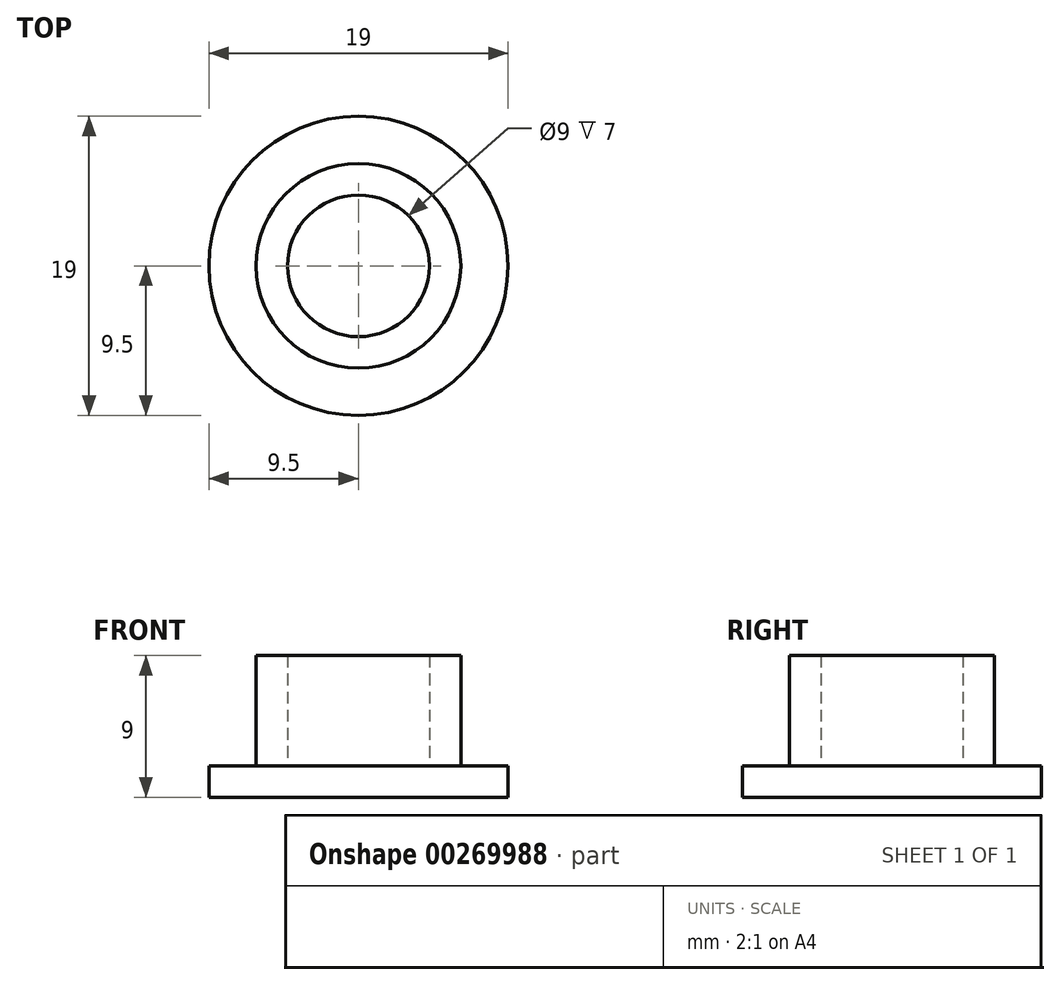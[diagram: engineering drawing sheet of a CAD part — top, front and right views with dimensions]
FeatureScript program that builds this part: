
annotation { "Feature Type Name" : "Feature", "Feature Type Description" : "" }
export const myFeature = defineFeature(function(context is Context, id is Id, definition is map)
    precondition{}
    {
        {
            var Q0;
            Q0=qCreatedBy(makeId("Top.planeOp"),FACE);
            var sketch = newSketch(context, id + "F0", { "sketchPlane" : qUnion([Q0])});
            skCircle(sketch, "E0", {"center": v(0, 0) * mm, "radius": 4.5 * mm});
            skCircle(sketch, "E1", {"center": v(0, 0) * mm, "radius": 6.5 * mm});
            skCircle(sketch, "E2", {"center": v(0, 0) * mm, "radius": 9.5 * mm});
            skSolve(sketch);
        }
        {
            var Q0;
            Q0=makeQuery(id+"F0.imprint","IMPRINT",FACE,{"disambiguationData":[TD([[makeQuery(id+"F0.imprint","IMPRINT",EDGE,{"derivedFrom":sQuery(id+"F0.wireOp",EDGE,"E1")}),-1.0]])]});
            extrude(context, id + "F1", {"entities" : qUnion([Q0]), "depth" : 2 * mm, "offsetDistance" : 25 * mm});
        }
        {
            var Q0;
            Q0=makeQuery(id+"F0.imprint","IMPRINT",FACE,{"disambiguationData":[TD([[makeQuery(id+"F0.imprint","IMPRINT",EDGE,{"derivedFrom":sQuery(id+"F0.wireOp",EDGE,"E0")}),-1.0]])]});
            extrude(context, id + "F2", {"entities" : qUnion([Q0]), "operationType" : NewBodyOperationType.ADD, "depth" : 9 * mm, "offsetDistance" : 25 * mm});
        }
        {
            var Q0;
            Q0=makeQuery(id+"F0.imprint","IMPRINT",FACE,{"disambiguationData":[TD([[makeQuery(id+"F0.imprint","IMPRINT",EDGE,{"derivedFrom":sQuery(id+"F0.wireOp",EDGE,"E0")}),1.0]])]});
            extrude(context, id + "F3", {"entities" : qUnion([Q0]), "operationType" : NewBodyOperationType.ADD, "depth" : 2 * mm, "offsetDistance" : 25 * mm});
        }
    });
